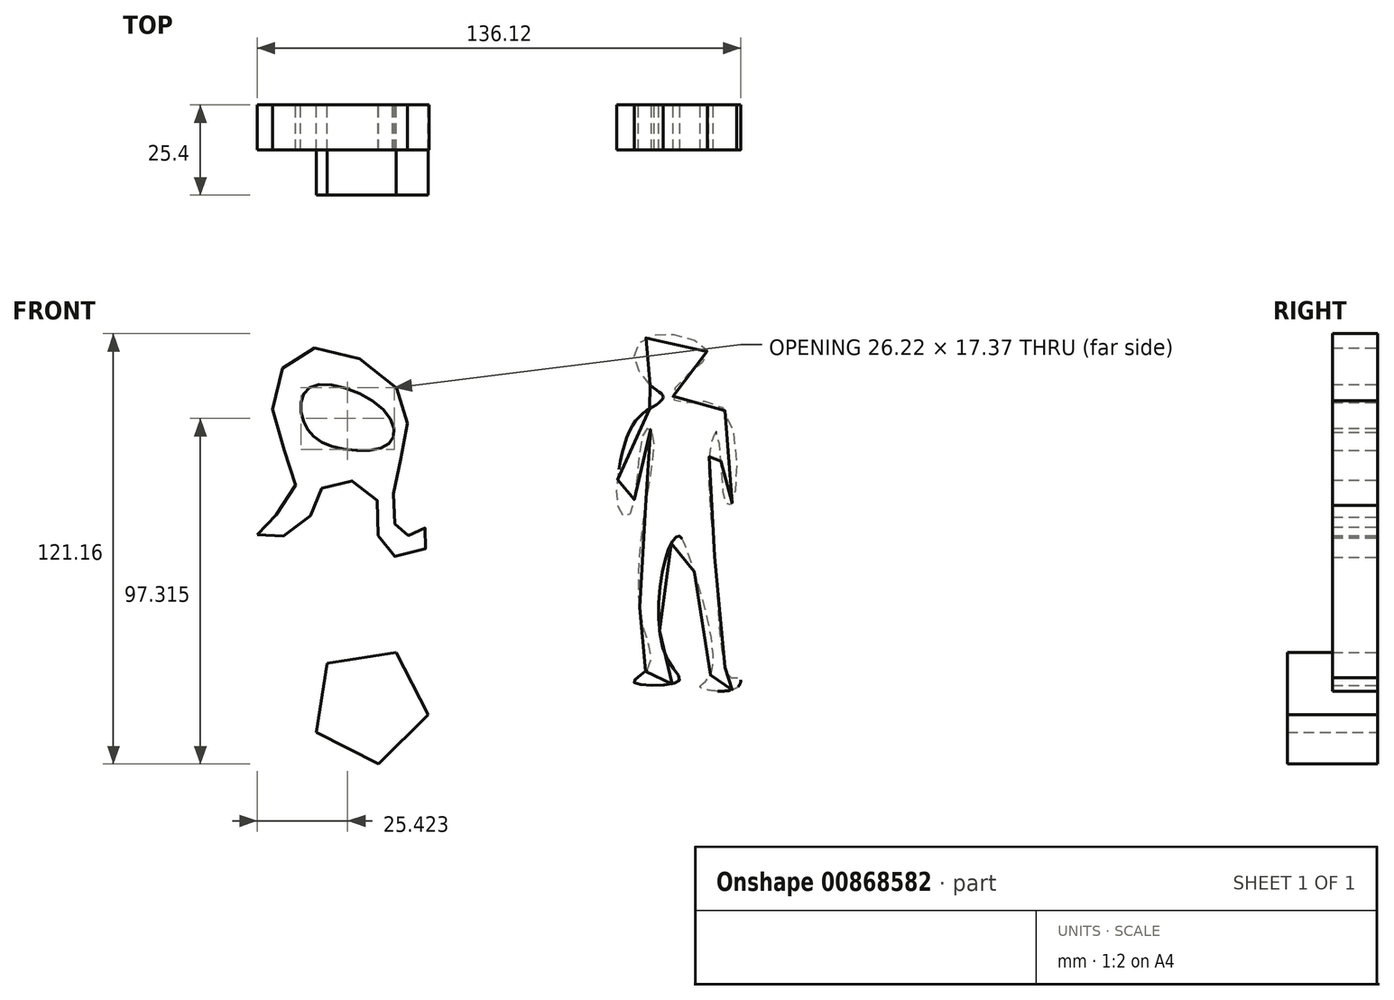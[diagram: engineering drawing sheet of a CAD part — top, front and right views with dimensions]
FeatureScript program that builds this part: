
annotation { "Feature Type Name" : "Feature", "Feature Type Description" : "" }
export const myFeature = defineFeature(function(context is Context, id is Id, definition is map)
    precondition{}
    {
        {
            var Q0;
            Q0=qCreatedBy(makeId("Front.planeOp"),FACE);
            var sketch = newSketch(context, id + "F0", { "sketchPlane" : qUnion([Q0])});
            skCircle(sketch, "E0.cCircle", {"center": v(-28.78, -50.13) * mm, "radius": 16.74 * mm, "construction": true});
            skLineSegment(sketch, "E0.0", {"start": v(-12.25, -52.74) * mm, "end": v(-26.15, -66.66) * mm});
            skLineSegment(sketch, "E0.1", {"start": v(-26.15, -66.66) * mm, "end": v(-43.69, -57.74) * mm});
            skLineSegment(sketch, "E0.2", {"start": v(-43.69, -57.74) * mm, "end": v(-40.62, -38.3) * mm});
            skLineSegment(sketch, "E0.3", {"start": v(-40.62, -38.3) * mm, "end": v(-21.2, -35.21) * mm});
            skLineSegment(sketch, "E0.4", {"start": v(-21.2, -35.21) * mm, "end": v(-12.25, -52.74) * mm});
            skSolve(sketch);
        }
        {
            var Q0;
            Q0 = qSketchRegion(id + "F0", true);
            extrude(context, id + "F1", {"entities" : qUnion([Q0]), "depth" : 25.4 * mm, "offsetDistance" : 25.4 * mm});
        }
        {
            var Q0;
            Q0=qCreatedBy(makeId("Front.planeOp"),FACE);
            var sketch = newSketch(context, id + "F2", { "sketchPlane" : qUnion([Q0])});
            skFitSpline(sketch, "E1", {"points": [v(50.23, 40.1) * mm, v(45.96, 49.7) * mm, v(54.85, 54.5) * mm, v(66.4, 48.98) * mm, v(57.7, 39.74) * mm, v(57.87, 35.3) * mm, v(70.5, 33.87) * mm, v(73.34, 6.85) * mm, v(72.1, 6.31) * mm, v(71.03, 8.98) * mm, v(69.08, 26.58) * mm, v(67.12, 21.42) * mm, v(68.72, -12) * mm, v(72.99, -42.23) * mm, v(75.48, -42.4) * mm, v(74.59, -45.25) * mm, v(64.45, -45.07) * mm, v(67.3, -41.52) * mm, v(60.9, -7.02) * mm, v(58.23, -2.4) * mm, v(54.85, -7.91) * mm, v(54.85, -36.54) * mm, v(58.23, -43.47) * mm, v(45.78, -43.65) * mm, v(49.87, -39.56) * mm, v(48.1, -26.76) * mm, v(48.98, 5.42) * mm, v(50.76, 27.11) * mm, v(48.8, 27.3) * mm, v(44.54, 3.64) * mm, v(41.87, 4.18) * mm, v(45.07, 28.18) * mm, v(52.36, 34.76) * mm, v(53.96, 36.9) * mm, v(50.23, 40.1) * mm]});
            skSolve(sketch);
        }
        {
            var Q0;
            Q0 = qSketchRegion(id + "F2", true);
            extrude(context, id + "F3", {"entities" : qUnion([Q0]), "depth" : 12.7 * mm, "offsetDistance" : 25.4 * mm});
        }
        {
            var Q0;
            Q0=qCreatedBy(makeId("Front.planeOp"),FACE);
            var sketch = newSketch(context, id + "F4", { "sketchPlane" : qUnion([Q0])});
            skFitSpline(sketch, "E2", {"points": [v(-60.28, -2.1) * mm, v(-50.08, 9.23) * mm, v(-55.6, 29.65) * mm, v(-47.01, 49.86) * mm, v(-20.45, 38.33) * mm, v(-19.91, 19.21) * mm, v(-22, 2.78) * mm, v(-18.35, -2.51) * mm, v(-13.5, 0) * mm, v(-12.7, -5.68) * mm, v(-25.02, -6.46) * mm, v(-27.23, 9.23) * mm, v(-41.29, 11.81) * mm, v(-47.73, 0) * mm, v(-60.28, -2.1) * mm]});
            skFitSpline(sketch, "E3", {"points": [v(-45.6, 39.34) * mm, v(-47.38, 30.05) * mm, v(-39.12, 22.74) * mm, v(-22.86, 23.92) * mm, v(-25.53, 33.76) * mm, v(-45.6, 39.34) * mm]});
            skSolve(sketch);
        }
        {
            var Q0;
            Q0=makeQuery(id+"F4.imprint","IMPRINT",FACE,{"disambiguationData":[TD([[makeQuery(id+"F4.imprint","IMPRINT",EDGE,{"derivedFrom":sQuery(id+"F4.wireOp",EDGE,"E2")}),-1.0]])]});
            extrude(context, id + "F5", {"entities" : qUnion([Q0]), "depth" : 12.7 * mm, "offsetDistance" : 25.4 * mm});
        }
    });
